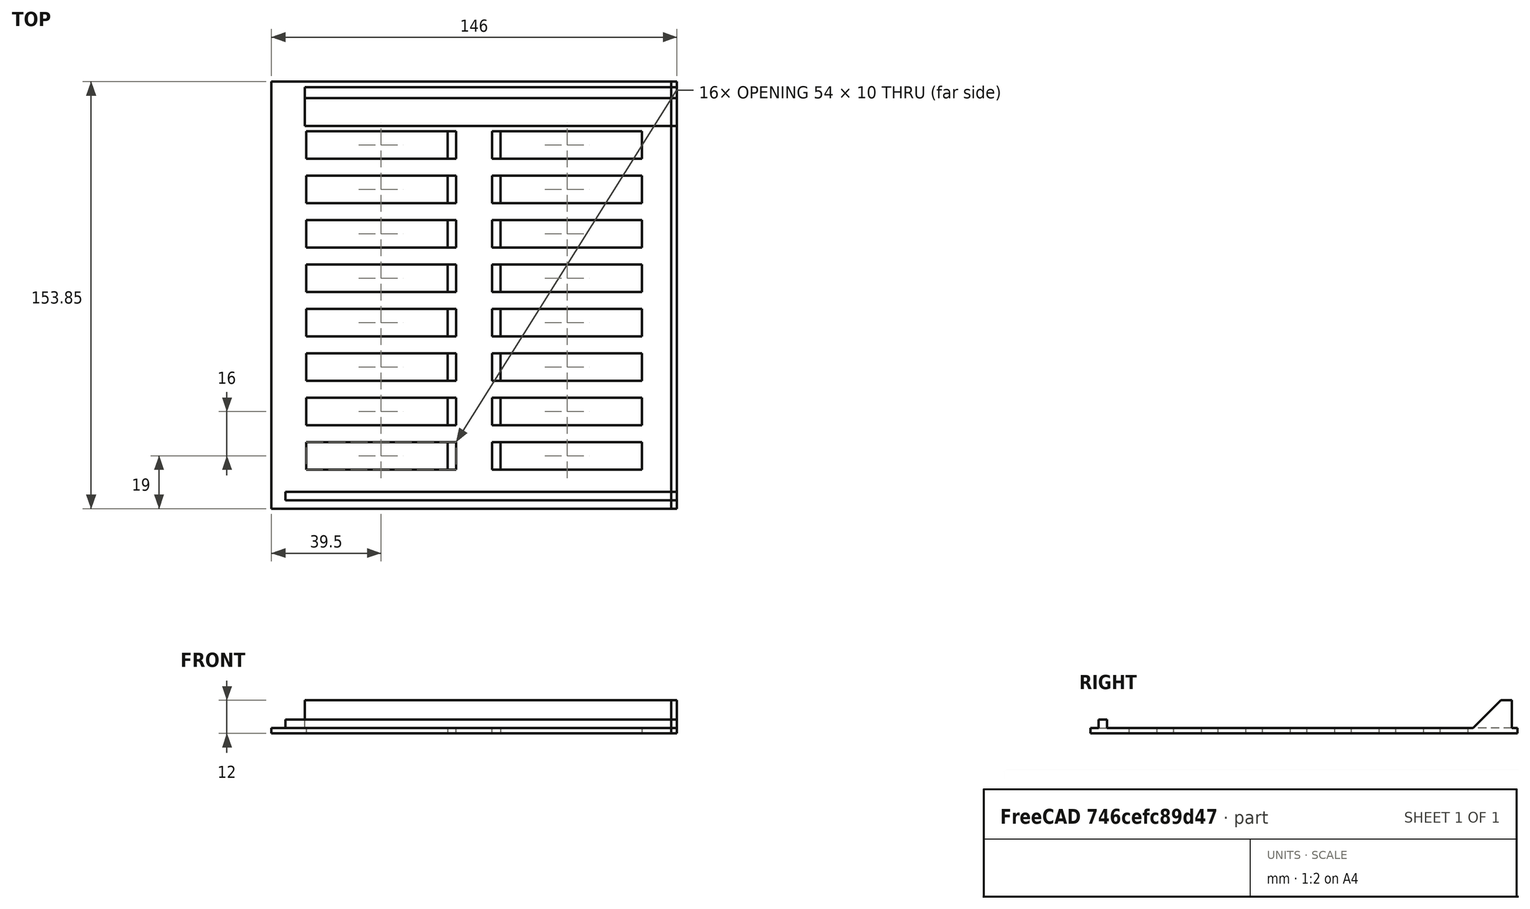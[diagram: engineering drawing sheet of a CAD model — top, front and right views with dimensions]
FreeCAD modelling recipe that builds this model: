
FCSTD DOCUMENT  (FreeCAD 0.17R13522 (Git))
Label: lateral_izquierdo_v3
License: CreativeCommons Attribution-ShareAlike
LicenseURL: http://creativecommons.org/licenses/by-sa/4.0/
objects: Part::Feature×6, Part::MultiFuse×4, Part::Box×2, Part::Cut×2, Part::FeaturePython×1
note: 15 computed .brp shape members not serialized (recipe doc carries the construction recipe); baked Part::Feature solids carry a one-line shape summary decoded from their .brp

FEATURE [Part::Feature] Cut001
  shape: bbox 30 x 153.9 x 12 mm, 47 faces (baked)
FEATURE [Part::Feature] Cut001001  label="Cut002"
  Placement = pos=(-32,0,0) rot=(0,0,1;0rad)
  shape: bbox 67 x 153.9 x 12 mm, 79 faces (baked)
FEATURE [Part::Feature] Cut001002
  Placement = pos=(-64,0,0) rot=(0,0,1;0rad)
  shape: bbox 47 x 153.9 x 12 mm, 47 faces (baked)
FEATURE [Part::Feature] Cut001003
  Placement = pos=(-34,0,0) rot=(0,0,1;0rad)
  shape: bbox 67 x 153.9 x 12 mm, 79 faces (baked)
FEATURE [Part::Feature] Cut001004
  Placement = pos=(-30,0,0) rot=(0,0,1;0rad)
  shape: bbox 67 x 153.9 x 12 mm, 79 faces (baked)
FEATURE [Part::MultiFuse] Fusion
  Shapes = -> [Cut001,Cut001001]
FEATURE [Part::MultiFuse] Fusion001
  Shapes = -> [Fusion,Cut001004]
FEATURE [Part::MultiFuse] Fusion002
  Shapes = -> [Fusion001,Cut001003]
FEATURE [Part::MultiFuse] Fusion003
  Shapes = -> [Fusion002,Cut001002]
FEATURE [Part::Feature] Fusion003001  label="Fusion004"
  shape: bbox 146 x 153.9 x 12 mm, 79 faces (baked)
FEATURE [Part::Box] Box  label="Cube"
  AttacherType = Attacher::AttachEngine3D
  Height = 10
  Length = 4.5
  Placement = pos=(63,14,-62) rot=(0,0,1;0rad)
  Width = 10
FEATURE [Part::FeaturePython] Array  # Draft array (typed FeaturePython)
  Angle = 360
  ArrayType = 0
  Axis = (0,0,1)
  Base = -> Box
  Center = (0,0,0)
  Fuse = false
  IntervalAxis = (0,0,0)
  IntervalX = (17.5,0,0)
  IntervalY = (0,16,0)
  IntervalZ = (0,0,0)
  NumberPolar = 1
  NumberX = 2
  NumberY = 8
  NumberZ = 1
  Placement = pos=(-1,0,0) rot=(0,0,1;0rad)
FEATURE [Part::Cut] Cut
  Base = -> Fusion003001
  Tool = -> Array
FEATURE [Part::Box] Box001  label="Cube001"
  AttacherType = Attacher::AttachEngine3D
  Height = 20
  Length = 14
  Placement = pos=(144,-23,-62) rot=(0,0,1;0rad)
  Width = 300
FEATURE [Part::Cut] Cut001005
  Base = -> Cut
  Tool = -> Box001
